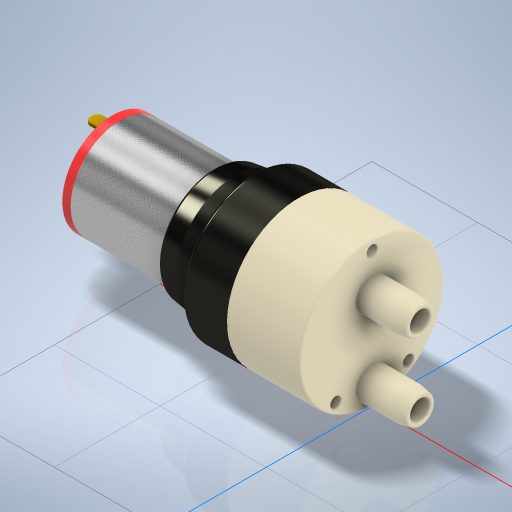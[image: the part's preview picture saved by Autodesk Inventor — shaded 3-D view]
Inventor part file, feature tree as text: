
AUTODESK INVENTOR PART (.ipt)
format: ipt  version: 2024 (Build 280153000, 153)  size: 491,008 bytes
history: native  units: in
note: dims shown in document units (in); Inventor stores cm internally (conversion verified against a paired STEP export)
features: extrude x6, sketch x6, plane x4, split x3, chamfer x3, fillet x3
ambient origin geometry x8: Origin, YZ Plane, XZ Plane, XY Plane, X Axis, Y Axis, Z Axis, Center Point
bodies: Solid1 (feature_tree), Solid2 (feature_tree), Solid3 (feature_tree), Solid4 (feature_tree), Solid5 (feature_tree), Solid6 (feature_tree), Solid7 (feature_tree), Solid8 (feature_tree), Solid9 (feature_tree)
feature tree (25):
  extrude  "Extrusion1"  Depth=1.1181in TaperAngle=0.0deg
  extrude  "Extrusion2"  Depth=0.374in TaperAngle=0.0deg
  extrude  "Extrusion3"  Depth=0.9606in TaperAngle=0.0deg
  extrude  "Extrusion4"  Depth=0.3031in
  extrude  "Extrusion5"  Depth=0.185in
  plane  "Work Plane1"
  plane  "Work Plane2"
  split  "Split4"
  plane  "Work Plane3"
  split  "Split5"
  extrude  "Extrusion6"  Depth=0.1969in
  chamfer  "Chamfer3"  Distance=0.4606in
  fillet  "Fillet1"  Radius=0.1024in
  plane  "Work Plane4"
  split  "Split6"
  fillet  "Fillet2"  Radius=0.1024in
  chamfer  "Chamfer1"  Distance=0.1024in
  chamfer  "Chamfer2"  Distance=0.0394in
  fillet  "Fillet3"  Radius=0.685in
  sketch  "Sketch1"  dims[d0=1.3583in d1=1.1181in d2=0.0in]
  sketch  "Sketch2"  dims[d3=1.1102in d4=0.374in d5=0.0in]
  sketch  "Sketch3"  dims[d6=0.9409in d7=0.9606in d8=0.0in]
  sketch  "Sketch5"  dims[d9=0.3031in d10=0.3031in]
  sketch  "Sketch6"  dims[d11=0.185in d12=0.185in]
  sketch  "Sketch8"  dims[d13=0.0413in d14=0.5906in d15=0.4606in d16=0.0in d17=0.1024in d18=0.1024in d19=0.1024in d20=0.0394in d21=0.685in d22=0.0394in d23=0.0394in d24=0.3937in d25=0.0in d26=-0.689in d27=-0.8031in d28=-0.0787in d29=0.1181in d30=0.0276in d31=0.0276in d32=0.3386in d33=0.3386in d34=0.1969in d35=0.0in d36=0.0394in d37=0.0in d38=0.0472in d39=0.0197in d40=0.1181in d41=45.0deg d42=0.0197in d43=0.1181in d44=45.0deg d45=0.0157in d46=0.0276in d47=0.1969in d48=45.0deg]
